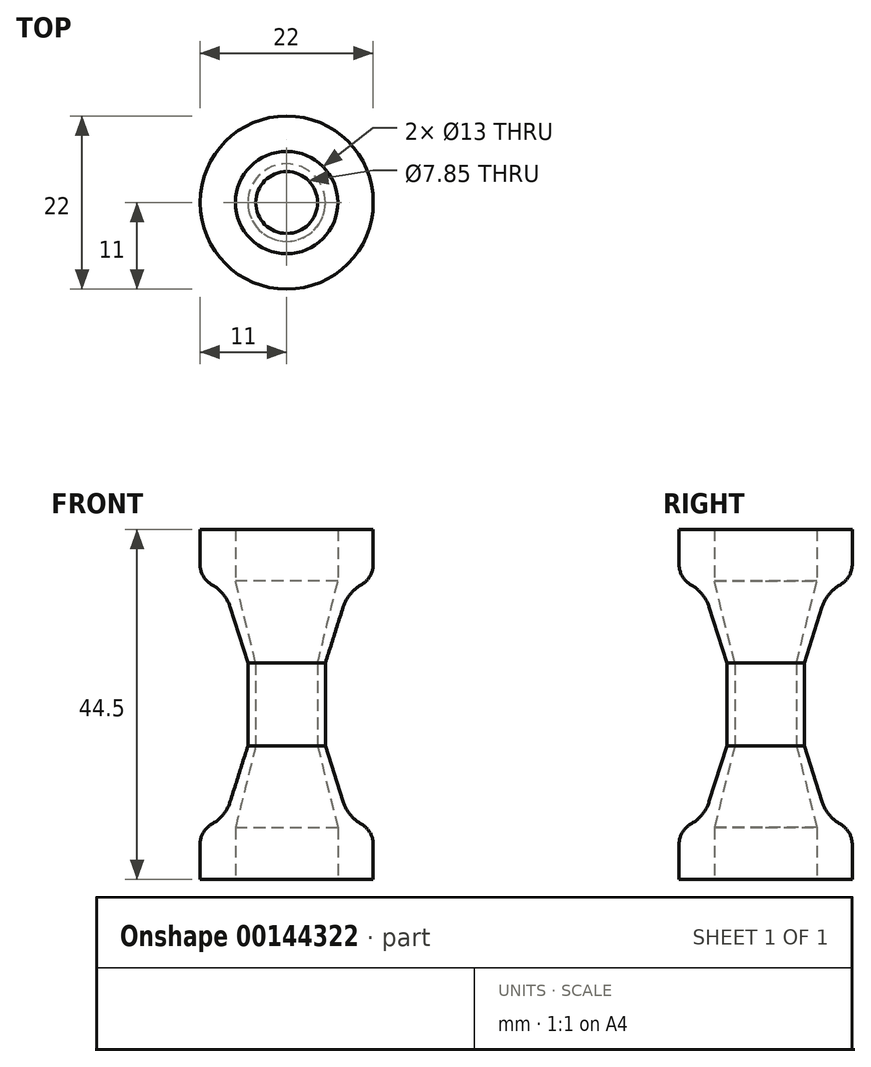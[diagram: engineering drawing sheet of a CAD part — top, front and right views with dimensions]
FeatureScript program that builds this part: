
annotation { "Feature Type Name" : "Feature", "Feature Type Description" : "" }
export const myFeature = defineFeature(function(context is Context, id is Id, definition is map)
    precondition{}
    {
        {
            var Q0;
            Q0=qCreatedBy(makeId("Top.planeOp"),FACE);
            var sketch = newSketch(context, id + "F0", { "sketchPlane" : qUnion([Q0])});
            skCircle(sketch, "E0", {"center": v(0, 0) * mm, "radius": 11 * mm});
            skCircle(sketch, "E1", {"center": v(0, 0) * mm, "radius": 6.5 * mm});
            skSolve(sketch);
        }
        {
            var Q0;
            Q0 = qSketchRegion(id + "F0", true);
            extrude(context, id + "F1", {"entities" : qUnion([Q0]), "depth" : 6.5 * mm});
        }
        {
            var Q0;
            Q0=makeQuery(id+"F1.opExtrude","CAP_FACE",FACE,{"disambiguationData":[OSD([sQuery(id+"F0.wireOp",EDGE,"E0"),sQuery(id+"F0.wireOp",EDGE,"E1")])],"isStart":false});
            var sketch = newSketch(context, id + "F2", { "sketchPlane" : qUnion([Q0])});
            skCircle(sketch, "E2", {"center": v(0, 0) * mm, "radius": 8.25 * mm});
            skCircle(sketch, "E3", {"center": v(0, 0) * mm, "radius": 3.92 * mm});
            skSolve(sketch);
        }
        {
            var Q0;
            Q0 = qSketchRegion(id + "F2", true);
            extrude(context, id + "F3", {"entities" : qUnion([Q0]), "operationType" : NewBodyOperationType.ADD, "depth" : 10.5 * mm});
        }
        {
            var Q0;
            Q0=makeQuery(id+"F3.opExtrude","CAP_FACE",FACE,{"disambiguationData":[OSD([sQuery(id+"F2.wireOp",EDGE,"E2"),sQuery(id+"F2.wireOp",EDGE,"E3")])],"isStart":false});
            var sketch = newSketch(context, id + "F4", { "sketchPlane" : qUnion([Q0])});
            skCircle(sketch, "E4", {"center": v(0, 0) * mm, "radius": 4.92 * mm});
            skCircle(sketch, "E5", {"center": v(0, 0) * mm, "radius": 3.92 * mm});
            skSolve(sketch);
        }
        {
            var Q0;
            Q0 = qSketchRegion(id + "F4", true);
            extrude(context, id + "F5", {"entities" : qUnion([Q0]), "operationType" : NewBodyOperationType.ADD, "depth" : 10.5 * mm});
        }
        {
            var Q0;
            Q0=makeQuery(id+"F5.opExtrude","CAP_FACE",FACE,{"disambiguationData":[OSD([sQuery(id+"F4.wireOp",EDGE,"E4"),sQuery(id+"F4.wireOp",EDGE,"E5")])],"isStart":false});
            var sketch = newSketch(context, id + "F6", { "sketchPlane" : qUnion([Q0])});
            skCircle(sketch, "E6.0", {"center": v(0, 0) * mm, "radius": 8.25 * mm});
            skCircle(sketch, "E7.0", {"center": v(0, 0) * mm, "radius": 3.92 * mm});
            skSolve(sketch);
        }
        {
            var Q0;
            Q0 = qSketchRegion(id + "F6", true);
            extrude(context, id + "F7", {"entities" : qUnion([Q0]), "operationType" : NewBodyOperationType.ADD, "depth" : 10.5 * mm});
        }
        {
            var Q0;
            Q0=makeQuery(id+"F7.opExtrude","CAP_FACE",FACE,{"disambiguationData":[OSD([sQuery(id+"F6.wireOp",EDGE,"E6.0"),sQuery(id+"F6.wireOp",EDGE,"E7.0")])],"isStart":false});
            var sketch = newSketch(context, id + "F8", { "sketchPlane" : qUnion([Q0])});
            skCircle(sketch, "E8.0", {"center": v(0, 0) * mm, "radius": 11 * mm});
            skCircle(sketch, "E9.0", {"center": v(0, 0) * mm, "radius": 6.5 * mm});
            skSolve(sketch);
        }
        {
            var Q0;
            Q0 = qSketchRegion(id + "F8", true);
            extrude(context, id + "F9", {"entities" : qUnion([Q0]), "operationType" : NewBodyOperationType.ADD, "depth" : 6.5 * mm});
        }
        {
            var Q0;
            Q0=makeQuery(id+"F3.opExtrude","CAP_EDGE",EDGE,{"disambiguationData":[OSD([sQuery(id+"F2.wireOp",EDGE,"E2")])],"isStart":false});
            chamfer(context, id + "F10", {"entities" : qUnion([Q0]), "chamferType" : ChamferType.TWO_OFFSETS, "width1" : 3.33 * mm, "oppositeDirection" : false, "width2" : 10.5 * mm, "tangentPropagation" : true});
        }
        {
            var Q0;
            Q0=makeQuery(id+"F7.opExtrude","CAP_EDGE",EDGE,{"disambiguationData":[OSD([sQuery(id+"F6.wireOp",EDGE,"E6.0")])],"isStart":true});
            chamfer(context, id + "F11", {"entities" : qUnion([Q0]), "chamferType" : ChamferType.TWO_OFFSETS, "width1" : 10.5 * mm, "oppositeDirection" : false, "width2" : 3.33 * mm, "tangentPropagation" : true});
        }
        {
            var Q0;
            Q0=makeQuery(id+"F3.opExtrude","CAP_EDGE",EDGE,{"disambiguationData":[OSD([sQuery(id+"F2.wireOp",EDGE,"E3")])],"isStart":true});
            var Q1;
            Q1=makeQuery(id+"F7.opExtrude","CAP_EDGE",EDGE,{"disambiguationData":[OSD([sQuery(id+"F6.wireOp",EDGE,"E7.0")])],"isStart":false});
            chamfer(context, id + "F12", {"entities" : qUnion([Q0, Q1]), "chamferType" : ChamferType.TWO_OFFSETS, "width1" : 2.6 * mm, "oppositeDirection" : false, "width2" : 10.5 * mm, "tangentPropagation" : true});
        }
        {
            var Q0;
            Q0=makeQuery(id+"F11.opChamfer","BLEND_EDGE",EDGE,{"blendedFrom":[makeQuery(id+"F7.opExtrude","CAP_EDGE",EDGE,{"disambiguationData":[OSD([sQuery(id+"F6.wireOp",EDGE,"E6.0")])],"isStart":true}),makeQuery(id+"F9.opExtrude","CAP_FACE",FACE,{"disambiguationData":[OSD([sQuery(id+"F8.wireOp",EDGE,"E8.0"),sQuery(id+"F8.wireOp",EDGE,"E9.0")])],"isStart":true})],"blendedInto":[makeQuery(id+"F9.opExtrude","CAP_FACE",FACE,{"disambiguationData":[OSD([sQuery(id+"F8.wireOp",EDGE,"E8.0"),sQuery(id+"F8.wireOp",EDGE,"E9.0")])],"isStart":true})]});
            var Q1;
            Q1=makeQuery(id+"F10.opChamfer","BLEND_EDGE",EDGE,{"blendedFrom":[makeQuery(id+"F3.opExtrude","CAP_EDGE",EDGE,{"disambiguationData":[OSD([sQuery(id+"F2.wireOp",EDGE,"E2")])],"isStart":false}),makeQuery(id+"F1.opExtrude","CAP_FACE",FACE,{"disambiguationData":[OSD([sQuery(id+"F0.wireOp",EDGE,"E0"),sQuery(id+"F0.wireOp",EDGE,"E1")])],"isStart":false})],"blendedInto":[makeQuery(id+"F1.opExtrude","CAP_FACE",FACE,{"disambiguationData":[OSD([sQuery(id+"F0.wireOp",EDGE,"E0"),sQuery(id+"F0.wireOp",EDGE,"E1")])],"isStart":false})]});
            fillet(context, id + "F13", {"entities" : qUnion([Q0, Q1]), "radius" : 5 * mm, "tangentPropagation" : true, "allowEdgeOverflow" : false});
        }
        {
            var Q0;
            {var subQ0=sQuery(id+"F8.wireOp",EDGE,"E8.0");Q0=makeQuery(id+"F13.opFillet","BLEND_EDGE",EDGE,{"blendedFrom":[makeQuery(id+"F11.opChamfer","BLEND_EDGE",EDGE,{"blendedFrom":[makeQuery(id+"F7.opExtrude","CAP_EDGE",EDGE,{"disambiguationData":[OSD([sQuery(id+"F6.wireOp",EDGE,"E6.0")])],"isStart":true}),makeQuery(id+"F9.opExtrude","CAP_FACE",FACE,{"disambiguationData":[OSD([subQ0,sQuery(id+"F8.wireOp",EDGE,"E9.0")])],"isStart":true})],"blendedInto":[makeQuery(id+"F9.opExtrude","CAP_FACE",FACE,{"disambiguationData":[OSD([subQ0,sQuery(id+"F8.wireOp",EDGE,"E9.0")])],"isStart":true})]}),makeQuery(id+"F9.opExtrude","SWEPT_FACE",FACE,{"disambiguationData":[OSD([subQ0])]})],"blendedInto":[makeQuery(id+"F9.opExtrude","SWEPT_FACE",FACE,{"disambiguationData":[OSD([subQ0])]})]});}
            var Q1;
            {var subQ0=sQuery(id+"F0.wireOp",EDGE,"E0");Q1=makeQuery(id+"F13.opFillet","BLEND_EDGE",EDGE,{"blendedFrom":[makeQuery(id+"F10.opChamfer","BLEND_EDGE",EDGE,{"blendedFrom":[makeQuery(id+"F3.opExtrude","CAP_EDGE",EDGE,{"disambiguationData":[OSD([sQuery(id+"F2.wireOp",EDGE,"E2")])],"isStart":false}),makeQuery(id+"F1.opExtrude","CAP_FACE",FACE,{"disambiguationData":[OSD([subQ0,sQuery(id+"F0.wireOp",EDGE,"E1")])],"isStart":false})],"blendedInto":[makeQuery(id+"F1.opExtrude","CAP_FACE",FACE,{"disambiguationData":[OSD([subQ0,sQuery(id+"F0.wireOp",EDGE,"E1")])],"isStart":false})]}),makeQuery(id+"F1.opExtrude","SWEPT_FACE",FACE,{"disambiguationData":[OSD([subQ0])]})],"blendedInto":[makeQuery(id+"F1.opExtrude","SWEPT_FACE",FACE,{"disambiguationData":[OSD([subQ0])]})]});}
            fillet(context, id + "F14", {"entities" : qUnion([Q0, Q1]), "radius" : 3 * mm, "tangentPropagation" : true, "allowEdgeOverflow" : false});
        }
    });
